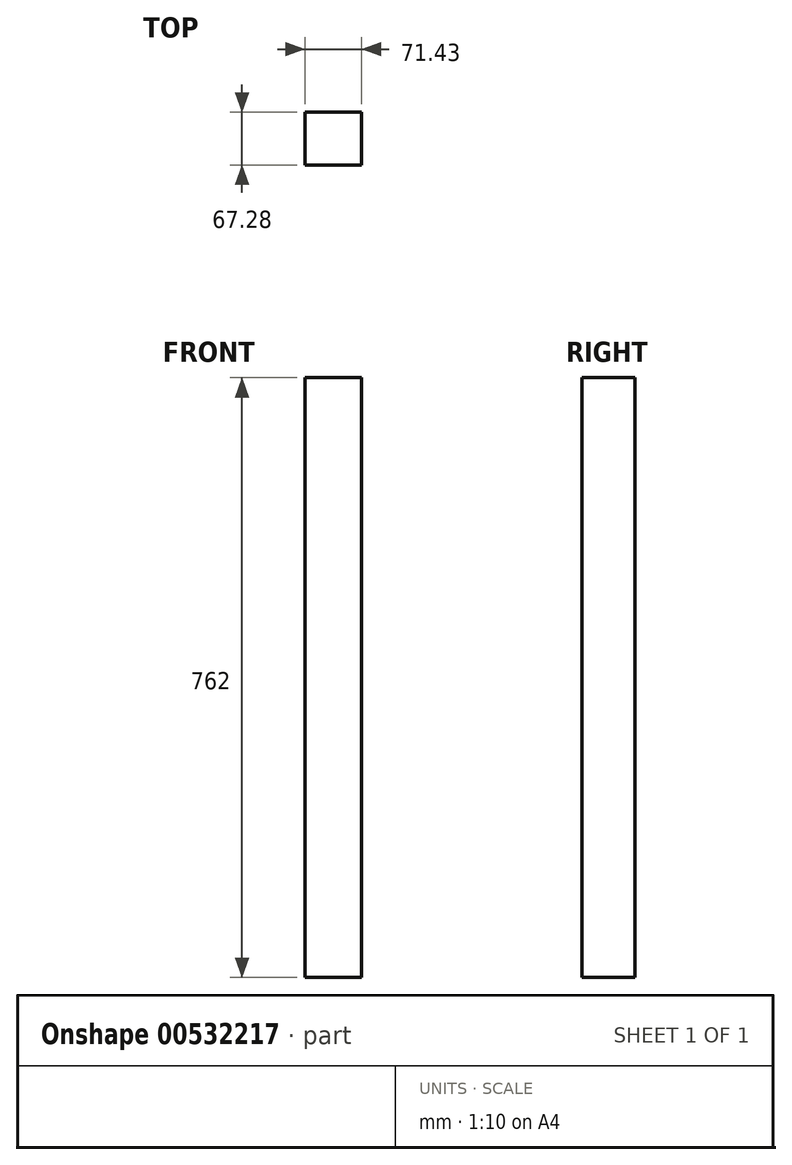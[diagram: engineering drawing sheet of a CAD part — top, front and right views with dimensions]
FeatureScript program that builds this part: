
annotation { "Feature Type Name" : "Feature", "Feature Type Description" : "" }
export const myFeature = defineFeature(function(context is Context, id is Id, definition is map)
    precondition{}
    {
        {
            var Q0;
            Q0=qCreatedBy(makeId("Top.planeOp"),FACE);
            var sketch = newSketch(context, id + "F0", { "sketchPlane" : qUnion([Q0])});
            skLineSegment(sketch, "E0.bottom", {"start": v(-30.26, 32.47) * mm, "end": v(41.17, 32.47) * mm});
            skLineSegment(sketch, "E0.top", {"start": v(-30.26, -34.81) * mm, "end": v(41.17, -34.81) * mm});
            skLineSegment(sketch, "E0.left", {"start": v(-30.26, 32.47) * mm, "end": v(-30.26, -34.81) * mm});
            skLineSegment(sketch, "E0.right", {"start": v(41.17, 32.47) * mm, "end": v(41.17, -34.81) * mm});
            skSolve(sketch);
        }
        {
            var Q0;
            Q0=makeQuery(id+"F0.imprint","IMPRINT",FACE,{"disambiguationData":[TD([[makeQuery(id+"F0.imprint","IMPRINT",EDGE,{"derivedFrom":sQuery(id+"F0.wireOp",EDGE,"E0.bottom")}),-1.0]])]});
            extrude(context, id + "F1", {"entities" : qUnion([Q0]), "depth" : 762 * mm, "offsetDistance" : 25.4 * mm});
        }
    });
